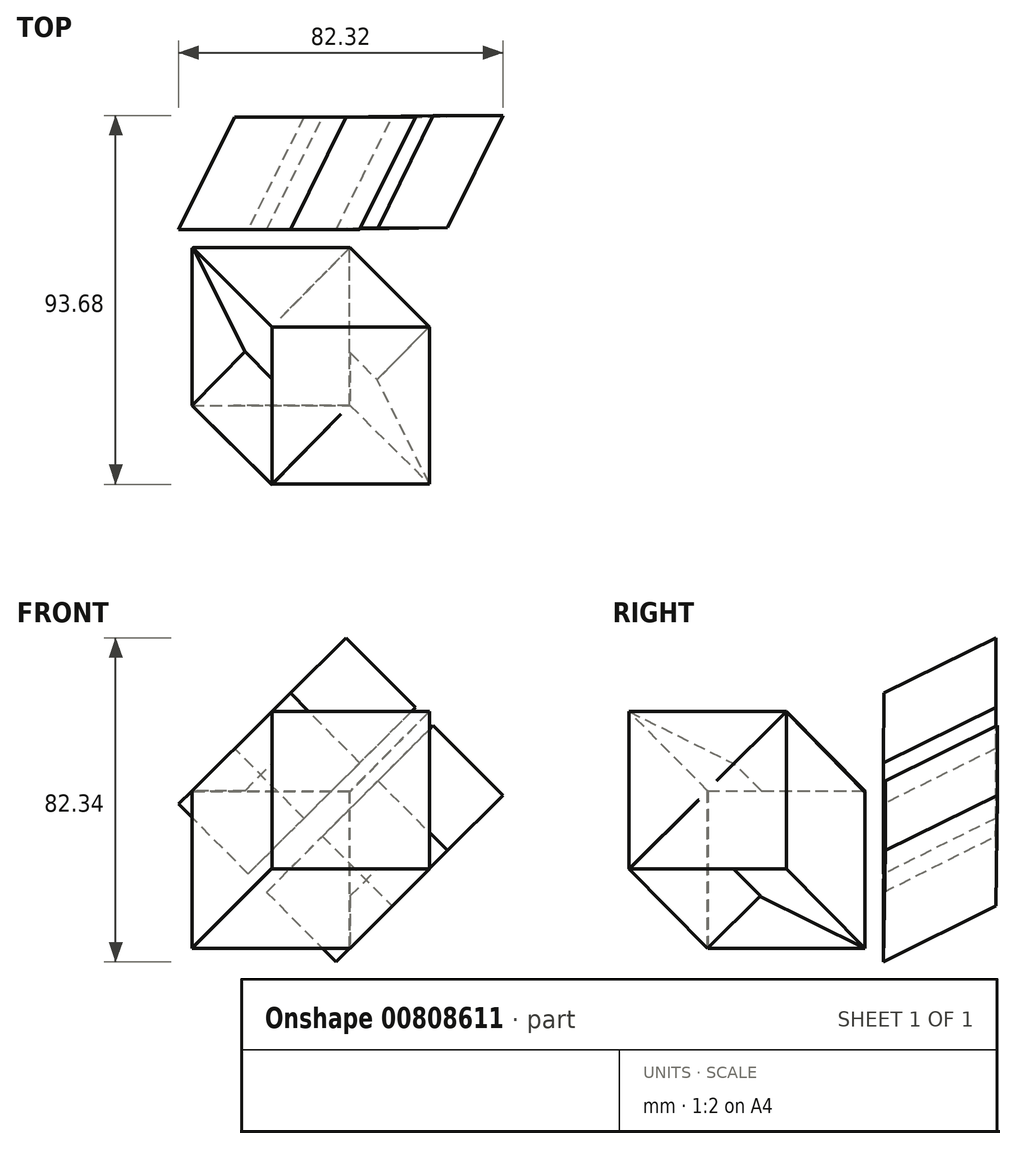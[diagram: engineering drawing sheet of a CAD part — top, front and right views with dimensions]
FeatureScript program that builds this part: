
annotation { "Feature Type Name" : "Feature", "Feature Type Description" : "" }
export const myFeature = defineFeature(function(context is Context, id is Id, definition is map)
    precondition{}
    {
        {
            var Q0;
            Q0=qCreatedBy(makeId("Front.planeOp"),FACE);
            var sketch = newSketch(context, id + "F0", { "sketchPlane" : qUnion([Q0])});
            skLineSegment(sketch, "E0.bottom", {"start": v(-16.4, 23.27) * mm, "end": v(23.6, 23.27) * mm});
            skLineSegment(sketch, "E0.top", {"start": v(-16.4, -16.73) * mm, "end": v(23.6, -16.73) * mm});
            skLineSegment(sketch, "E0.left", {"start": v(-16.4, 23.27) * mm, "end": v(-16.4, -16.73) * mm});
            skLineSegment(sketch, "E0.right", {"start": v(23.6, 23.27) * mm, "end": v(23.6, -16.73) * mm});
            skSolve(sketch);
        }
        {
            var Q0;
            Q0=makeQuery(id+"F0.imprint","IMPRINT",FACE,{"disambiguationData":[TD([[makeQuery(id+"F0.imprint","IMPRINT",EDGE,{"derivedFrom":sQuery(id+"F0.wireOp",EDGE,"E0.bottom")}),-1.0]])]});
            extrude(context, id + "F1", {"entities" : qUnion([Q0]), "depth" : 40 * mm, "offsetDistance" : 25 * mm});
        }
        {
            var Q0;
            Q0=makeQuery(id+"F1.opExtrude","CAP_FACE",FACE,{"disambiguationData":[OSD([sQuery(id+"F0.wireOp",EDGE,"E0.bottom"),sQuery(id+"F0.wireOp",EDGE,"E0.top"),sQuery(id+"F0.wireOp",EDGE,"E0.left"),sQuery(id+"F0.wireOp",EDGE,"E0.right")])],"isStart":false});
            cPlane(context, id + "F2", {"entities" : qUnion([Q0]), "cplaneType" : CPlaneType.OFFSET, "offset" : 20 * mm, "oppositeDirection" : true, "width" : 150 * mm, "height" : 150 * mm});
        }
        {
            var Q0;
            Q0=qCreatedBy(id+"F2.planeOp",FACE);
            var sketch = newSketch(context, id + "F3", { "sketchPlane" : qUnion([Q0])});
            skLineSegment(sketch, "E1.bottom", {"start": v(3.87, 43.4) * mm, "end": v(43.87, 43.4) * mm});
            skLineSegment(sketch, "E1.top", {"start": v(3.87, 3.4) * mm, "end": v(43.87, 3.4) * mm});
            skLineSegment(sketch, "E1.left", {"start": v(3.87, 43.4) * mm, "end": v(3.87, 3.4) * mm});
            skLineSegment(sketch, "E1.right", {"start": v(43.87, 43.4) * mm, "end": v(43.87, 3.4) * mm});
            skSolve(sketch);
        }
        {
            var Q0;
            Q0=makeQuery(id+"F3.imprint","IMPRINT",FACE,{"disambiguationData":[TD([[makeQuery(id+"F3.imprint","IMPRINT",EDGE,{"derivedFrom":sQuery(id+"F3.wireOp",EDGE,"E1.bottom")}),-1.0]])]});
            extrude(context, id + "F4", {"entities" : qUnion([Q0]), "operationType" : NewBodyOperationType.ADD, "depth" : 40 * mm, "offsetDistance" : 25 * mm});
        }
        {
            var Q0;
            Q0=makeQuery(id+"F4.opExtrude","CAP_VERTEX",VERTEX,{"disambiguationData":[OSD([sQuery(id+"F3.wireOp",EDGE,"E1.bottom"),sQuery(id+"F3.wireOp",EDGE,"E1.left")])],"isStart":false});
            var Q1;
            Q1=makeQuery(id+"F1.opExtrude","CAP_VERTEX",VERTEX,{"disambiguationData":[OSD([sQuery(id+"F0.wireOp",EDGE,"E0.bottom"),sQuery(id+"F0.wireOp",EDGE,"E0.left")])],"isStart":false});
            var Q2;
            Q2=makeQuery(id+"F1.opExtrude","CAP_VERTEX",VERTEX,{"disambiguationData":[OSD([sQuery(id+"F0.wireOp",EDGE,"E0.top"),sQuery(id+"F0.wireOp",EDGE,"E0.left")])],"isStart":false});
            cPlane(context, id + "F5", {"entities" : qUnion([Q0, Q1, Q2]), "cplaneType" : CPlaneType.THREE_POINT, "offset" : 25 * mm, "width" : 150 * mm, "height" : 150 * mm});
        }
        {
            var Q0;
            Q0=qCreatedBy(id+"F5.planeOp",FACE);
            var sketch = newSketch(context, id + "F6", { "sketchPlane" : qUnion([Q0])});
            skLineSegment(sketch, "E2", {"start": v(-16.36, -16.66) * mm, "end": v(-44.9, 3.49) * mm});
            skLineSegment(sketch, "E3", {"start": v(-16.36, 23.26) * mm, "end": v(-44.9, 43.41) * mm});
            skLineSegment(sketch, "E4", {"start": v(-16.36, -16.66) * mm, "end": v(-16.36, 23.26) * mm});
            skLineSegment(sketch, "E5", {"start": v(-44.9, 3.49) * mm, "end": v(-44.9, 43.41) * mm});
            skSolve(sketch);
        }
        {
            var Q0;
            Q0=makeQuery(id+"F6.imprint","IMPRINT",FACE,{"disambiguationData":[TD([[makeQuery(id+"F6.imprint","IMPRINT",EDGE,{"derivedFrom":sQuery(id+"F6.wireOp",EDGE,"E2")}),-1.0]])]});
            extrude(context, id + "F7", {"entities" : qUnion([Q0]), "operationType" : NewBodyOperationType.ADD, "depth" : 25 * mm, "offsetDistance" : 25 * mm});
        }
        {
            var Q0;
            Q0=makeQuery(id+"F7.boolean.opBoolean","INTERSECT",VERTEX,{"derivedFrom":[makeQuery(id+"F1.opExtrude","SWEPT_FACE",FACE,{"disambiguationData":[OSD([sQuery(id+"F0.wireOp",EDGE,"E0.left")])]}),makeQuery(id+"F1.opExtrude","SWEPT_FACE",FACE,{"disambiguationData":[OSD([sQuery(id+"F0.wireOp",EDGE,"E0.bottom")])]}),makeQuery(id+"F7.opExtrude","SWEPT_FACE",FACE,{"disambiguationData":[OSD([sQuery(id+"F6.wireOp",EDGE,"E3")])]})]});
            var Q1;
            Q1=makeQuery(id+"F7.opExtrude","CAP_VERTEX",VERTEX,{"disambiguationData":[OSD([sQuery(id+"F6.wireOp",EDGE,"E3"),sQuery(id+"F6.wireOp",EDGE,"E5")])],"isStart":true});
            var Q2;
            Q2=makeQuery(id+"F4.opExtrude","CAP_VERTEX",VERTEX,{"disambiguationData":[OSD([sQuery(id+"F3.wireOp",EDGE,"E1.bottom"),sQuery(id+"F3.wireOp",EDGE,"E1.left")])],"isStart":true});
            cPlane(context, id + "F8", {"entities" : qUnion([Q0, Q1, Q2]), "cplaneType" : CPlaneType.THREE_POINT, "offset" : 25 * mm, "width" : 150 * mm, "height" : 150 * mm});
        }
        {
            var Q0;
            Q0=qCreatedBy(id+"F8.planeOp",FACE);
            var sketch = newSketch(context, id + "F9", { "sketchPlane" : qUnion([Q0])});
            skLineSegment(sketch, "E6", {"start": v(33.24, 20) * mm, "end": v(4.76, 0) * mm});
            skLineSegment(sketch, "E7", {"start": v(33.24, 59.91) * mm, "end": v(4.76, 39.98) * mm});
            skLineSegment(sketch, "E8", {"start": v(33.24, 20) * mm, "end": v(33.24, 59.91) * mm});
            skLineSegment(sketch, "E9", {"start": v(4.76, 0) * mm, "end": v(4.76, 39.98) * mm});
            skSolve(sketch);
        }
        {
            var Q0;
            Q0=makeQuery(id+"F9.imprint","IMPRINT",FACE,{"disambiguationData":[TD([[makeQuery(id+"F9.imprint","IMPRINT",EDGE,{"derivedFrom":sQuery(id+"F9.wireOp",EDGE,"E6")}),-1.0]])]});
            extrude(context, id + "F10", {"entities" : qUnion([Q0]), "operationType" : NewBodyOperationType.ADD, "depth" : 25 * mm, "offsetDistance" : 25 * mm});
        }
        {
            var Q0;
            Q0=makeQuery(id+"F4.opExtrude","CAP_VERTEX",VERTEX,{"disambiguationData":[OSD([sQuery(id+"F3.wireOp",EDGE,"E1.bottom"),sQuery(id+"F3.wireOp",EDGE,"E1.left")])],"isStart":true});
            var Q1;
            Q1=makeQuery(id+"F4.opExtrude","CAP_VERTEX",VERTEX,{"disambiguationData":[OSD([sQuery(id+"F3.wireOp",EDGE,"E1.bottom"),sQuery(id+"F3.wireOp",EDGE,"E1.right")])],"isStart":true});
            var Q2;
            Q2=makeQuery(id+"F1.opExtrude","CAP_VERTEX",VERTEX,{"disambiguationData":[OSD([sQuery(id+"F0.wireOp",EDGE,"E0.bottom"),sQuery(id+"F0.wireOp",EDGE,"E0.right")])],"isStart":true});
            cPlane(context, id + "F11", {"entities" : qUnion([Q0, Q1, Q2]), "cplaneType" : CPlaneType.THREE_POINT, "offset" : 25 * mm, "width" : 150 * mm, "height" : 150 * mm});
        }
        {
            var Q0;
            Q0=qCreatedBy(id+"F11.planeOp",FACE);
            var sketch = newSketch(context, id + "F12", { "sketchPlane" : qUnion([Q0])});
            skLineSegment(sketch, "E10", {"start": v(43.87, 44.89) * mm, "end": v(23.72, 16.36) * mm});
            skLineSegment(sketch, "E11", {"start": v(3.94, 44.89) * mm, "end": v(-16.2, 16.36) * mm});
            skLineSegment(sketch, "E12", {"start": v(43.87, 44.89) * mm, "end": v(3.94, 44.89) * mm});
            skLineSegment(sketch, "E13", {"start": v(23.72, 16.36) * mm, "end": v(-16.2, 16.36) * mm});
            skSolve(sketch);
        }
        {
            var Q0;
            Q0=makeQuery(id+"F12.imprint","IMPRINT",FACE,{"disambiguationData":[TD([[makeQuery(id+"F12.imprint","IMPRINT",EDGE,{"derivedFrom":sQuery(id+"F12.wireOp",EDGE,"E10")}),-1.0]])]});
            extrude(context, id + "F13", {"entities" : qUnion([Q0]), "operationType" : NewBodyOperationType.ADD, "depth" : 25 * mm, "offsetDistance" : 25 * mm});
        }
        {
            var Q0;
            {var subQ0=sQuery(id+"F3.wireOp",EDGE,"E1.right");Q0=makeQuery(id+"F13.boolean.opBoolean","INTERSECT",VERTEX,{"derivedFrom":[makeQuery(id+"F4.opExtrude","SWEPT_FACE",FACE,{"disambiguationData":[OSD([subQ0])]}),makeQuery(id+"F4.opExtrude","CAP_FACE",FACE,{"disambiguationData":[OSD([sQuery(id+"F3.wireOp",EDGE,"E1.bottom"),sQuery(id+"F3.wireOp",EDGE,"E1.top"),sQuery(id+"F3.wireOp",EDGE,"E1.left"),subQ0])],"isStart":true}),makeQuery(id+"F13.opExtrude","SWEPT_FACE",FACE,{"disambiguationData":[OSD([sQuery(id+"F12.wireOp",EDGE,"E10")])]})]});}
            var Q1;
            Q1=makeQuery(id+"F4.opExtrude","CAP_VERTEX",VERTEX,{"disambiguationData":[OSD([sQuery(id+"F3.wireOp",EDGE,"E1.top"),sQuery(id+"F3.wireOp",EDGE,"E1.right")])],"isStart":true});
            var Q2;
            Q2=makeQuery(id+"F1.opExtrude","CAP_VERTEX",VERTEX,{"disambiguationData":[OSD([sQuery(id+"F0.wireOp",EDGE,"E0.top"),sQuery(id+"F0.wireOp",EDGE,"E0.right")])],"isStart":true});
            cPlane(context, id + "F14", {"entities" : qUnion([Q0, Q1, Q2]), "cplaneType" : CPlaneType.THREE_POINT, "offset" : 25 * mm, "width" : 150 * mm, "height" : 150 * mm});
        }
        {
            var Q0;
            Q0=qCreatedBy(id+"F14.planeOp",FACE);
            var sketch = newSketch(context, id + "F15", { "sketchPlane" : qUnion([Q0])});
            skLineSegment(sketch, "E14", {"start": v(45.27, 3.4) * mm, "end": v(16.78, -16.76) * mm});
            skLineSegment(sketch, "E15", {"start": v(45.27, 43.4) * mm, "end": v(16.78, 23.08) * mm});
            skLineSegment(sketch, "E16", {"start": v(45.27, 3.4) * mm, "end": v(45.27, 43.4) * mm});
            skLineSegment(sketch, "E17", {"start": v(16.78, -16.76) * mm, "end": v(16.78, 23.08) * mm});
            skSolve(sketch);
        }
        {
            var Q0;
            Q0=makeQuery(id+"F15.imprint","IMPRINT",FACE,{"disambiguationData":[TD([[makeQuery(id+"F15.imprint","IMPRINT",EDGE,{"derivedFrom":sQuery(id+"F15.wireOp",EDGE,"E14")}),-1.0]])]});
            extrude(context, id + "F16", {"entities" : qUnion([Q0]), "operationType" : NewBodyOperationType.ADD, "depth" : 25 * mm, "offsetDistance" : 25 * mm});
        }
        {
            var Q0;
            Q0=makeQuery(id+"F4.opExtrude","CAP_VERTEX",VERTEX,{"disambiguationData":[OSD([sQuery(id+"F3.wireOp",EDGE,"E1.top"),sQuery(id+"F3.wireOp",EDGE,"E1.right")])],"isStart":false});
            var Q1;
            Q1=makeQuery(id+"F1.opExtrude","CAP_VERTEX",VERTEX,{"disambiguationData":[OSD([sQuery(id+"F0.wireOp",EDGE,"E0.top"),sQuery(id+"F0.wireOp",EDGE,"E0.left")])],"isStart":false});
            var Q2;
            Q2=makeQuery(id+"F1.opExtrude","CAP_VERTEX",VERTEX,{"disambiguationData":[OSD([sQuery(id+"F0.wireOp",EDGE,"E0.top"),sQuery(id+"F0.wireOp",EDGE,"E0.right")])],"isStart":false});
            cPlane(context, id + "F17", {"entities" : qUnion([Q0, Q1, Q2]), "cplaneType" : CPlaneType.THREE_POINT, "offset" : 25 * mm, "width" : 150 * mm, "height" : 150 * mm});
        }
        {
            var Q0;
            Q0=qCreatedBy(id+"F17.planeOp",FACE);
            var sketch = newSketch(context, id + "F18", { "sketchPlane" : qUnion([Q0])});
            skLineSegment(sketch, "E18", {"start": v(16.4, 16.34) * mm, "end": v(-23.73, 16.28) * mm});
            skLineSegment(sketch, "E19", {"start": v(-3.8, 44.72) * mm, "end": v(-43.92, 44.67) * mm});
            skLineSegment(sketch, "E20", {"start": v(16.4, 16.34) * mm, "end": v(-3.8, 44.72) * mm});
            skLineSegment(sketch, "E21", {"start": v(-23.73, 16.28) * mm, "end": v(-43.92, 44.67) * mm});
            skSolve(sketch);
        }
        {
            var Q0;
            Q0=makeQuery(id+"F18.imprint","IMPRINT",FACE,{"disambiguationData":[TD([[makeQuery(id+"F18.imprint","IMPRINT",EDGE,{"derivedFrom":sQuery(id+"F18.wireOp",EDGE,"E18")}),-1.0]])]});
            extrude(context, id + "F19", {"entities" : qUnion([Q0]), "operationType" : NewBodyOperationType.ADD, "depth" : 25 * mm, "offsetDistance" : 25 * mm});
        }
        {
            var Q0;
            Q0=makeQuery(id+"F19.opExtrude","CAP_VERTEX",VERTEX,{"disambiguationData":[OSD([sQuery(id+"F18.wireOp",EDGE,"E19"),sQuery(id+"F18.wireOp",EDGE,"E21")])],"isStart":true});
            var Q1;
            Q1=makeQuery(id+"F16.opExtrude","CAP_VERTEX",VERTEX,{"disambiguationData":[OSD([sQuery(id+"F15.wireOp",EDGE,"E14"),sQuery(id+"F15.wireOp",EDGE,"E16")])],"isStart":true});
            var Q2;
            Q2=makeQuery(id+"F19.opExtrude","CAP_VERTEX",VERTEX,{"disambiguationData":[OSD([sQuery(id+"F18.wireOp",EDGE,"E18"),sQuery(id+"F18.wireOp",EDGE,"E21")])],"isStart":true});
            cPlane(context, id + "F20", {"entities" : qUnion([Q0, Q1, Q2]), "cplaneType" : CPlaneType.THREE_POINT, "offset" : 25 * mm, "width" : 150 * mm, "height" : 150 * mm});
        }
        {
            var Q0;
            Q0=qCreatedBy(id+"F20.planeOp",FACE);
            var sketch = newSketch(context, id + "F21", { "sketchPlane" : qUnion([Q0])});
            skLineSegment(sketch, "E22", {"start": v(4.7, 0) * mm, "end": v(5.14, 40.02) * mm});
            skLineSegment(sketch, "E23", {"start": v(33.18, 20.1) * mm, "end": v(33.62, 59.9) * mm});
            skLineSegment(sketch, "E24", {"start": v(4.7, 0) * mm, "end": v(33.18, 20.1) * mm});
            skLineSegment(sketch, "E25", {"start": v(5.14, 40.02) * mm, "end": v(33.62, 59.9) * mm});
            skSolve(sketch);
        }
        {
            var Q0;
            Q0=makeQuery(id+"F21.imprint","IMPRINT",FACE,{"disambiguationData":[TD([[makeQuery(id+"F21.imprint","IMPRINT",EDGE,{"derivedFrom":sQuery(id+"F21.wireOp",EDGE,"E22")}),-1.0]])]});
            extrude(context, id + "F22", {"entities" : qUnion([Q0]), "oppositeDirection" : true, "depth" : 25 * mm, "offsetDistance" : 25 * mm});
        }
    });
